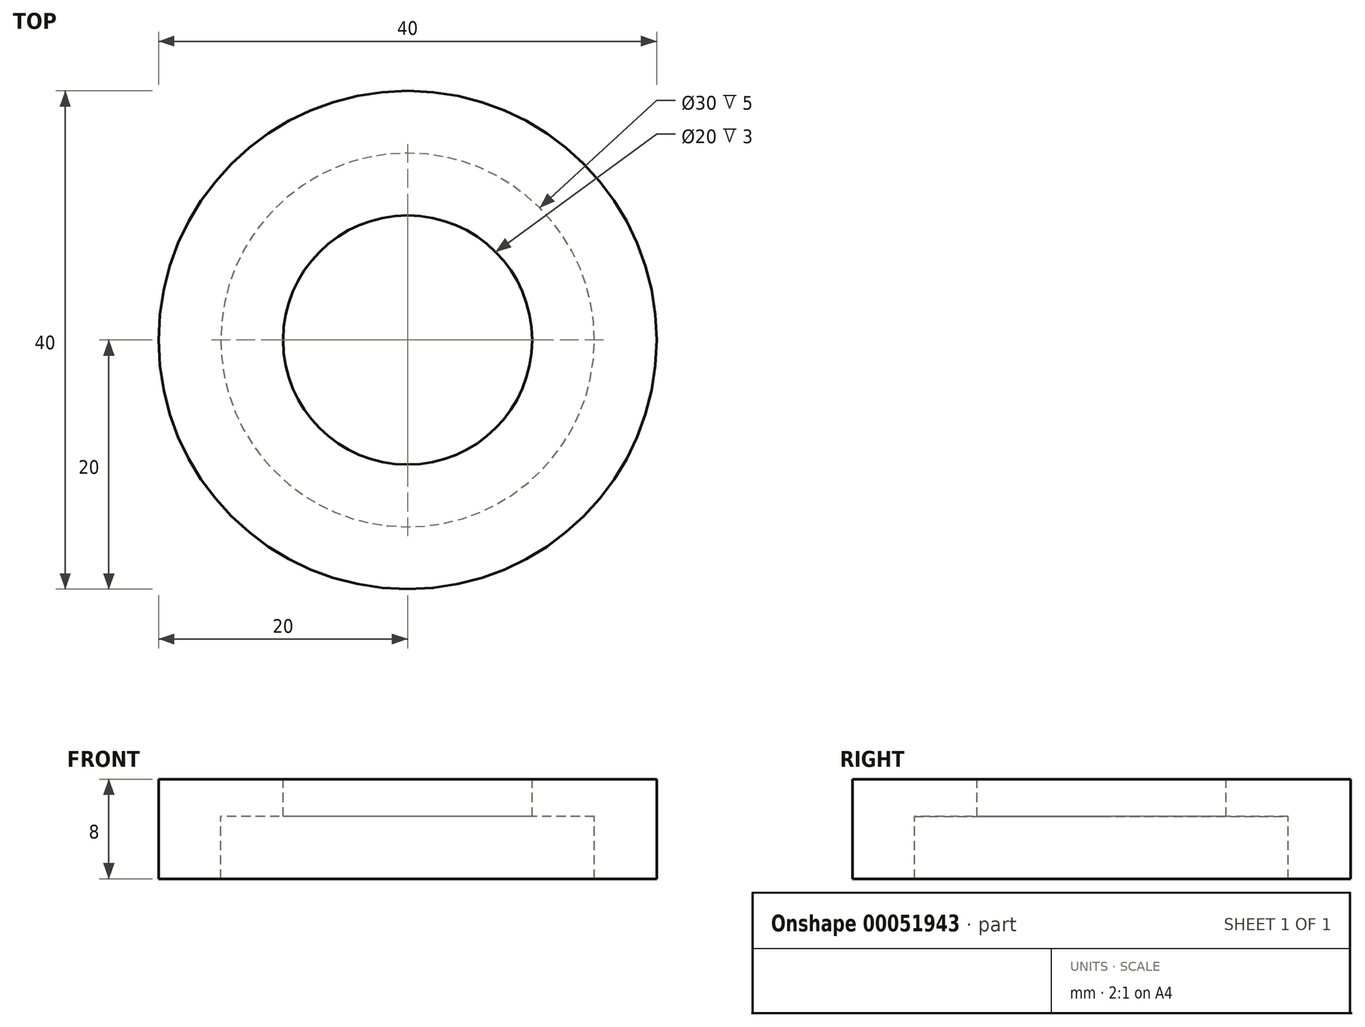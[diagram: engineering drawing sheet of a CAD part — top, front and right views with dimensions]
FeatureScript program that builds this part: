
annotation { "Feature Type Name" : "Feature", "Feature Type Description" : "" }
export const myFeature = defineFeature(function(context is Context, id is Id, definition is map)
    precondition{}
    {
        {
            var Q0;
            Q0=qCreatedBy(makeId("Front.planeOp"),FACE);
            var sketch = newSketch(context, id + "F0", { "sketchPlane" : qUnion([Q0])});
            skLineSegment(sketch, "E0", {"start": v(-20, 0) * mm, "end": v(-15, 0) * mm});
            skLineSegment(sketch, "E1", {"start": v(-15, 0) * mm, "end": v(-15, 5) * mm});
            skLineSegment(sketch, "E2", {"start": v(-15, 5) * mm, "end": v(-10, 5) * mm});
            skLineSegment(sketch, "E3", {"start": v(-10, 5) * mm, "end": v(-10, 8) * mm});
            skLineSegment(sketch, "E4", {"start": v(-10, 8) * mm, "end": v(-20, 8) * mm});
            skLineSegment(sketch, "E5", {"start": v(-20, 8) * mm, "end": v(-20, 0) * mm});
            skLineSegment(sketch, "E6", {"start": v(0, 0) * mm, "end": v(0, -26.4) * mm, "construction": true});
            skSolve(sketch);
        }
        {
            var Q0;
            Q0=makeQuery(id+"F0.imprint","IMPRINT",FACE,{"disambiguationData":[TD([[makeQuery(id+"F0.imprint","IMPRINT",EDGE,{"derivedFrom":sQuery(id+"F0.wireOp",EDGE,"E0")}),1.0]])]});
            var Q1;
            Q1=sQuery(id+"F0.wireOp",EDGE,"E6");
            revolve(context, id + "F1", {"entities" : qUnion([Q0]), "axis" : qUnion([Q1]), "revolveType" : RevolveType.FULL});
        }
    });
